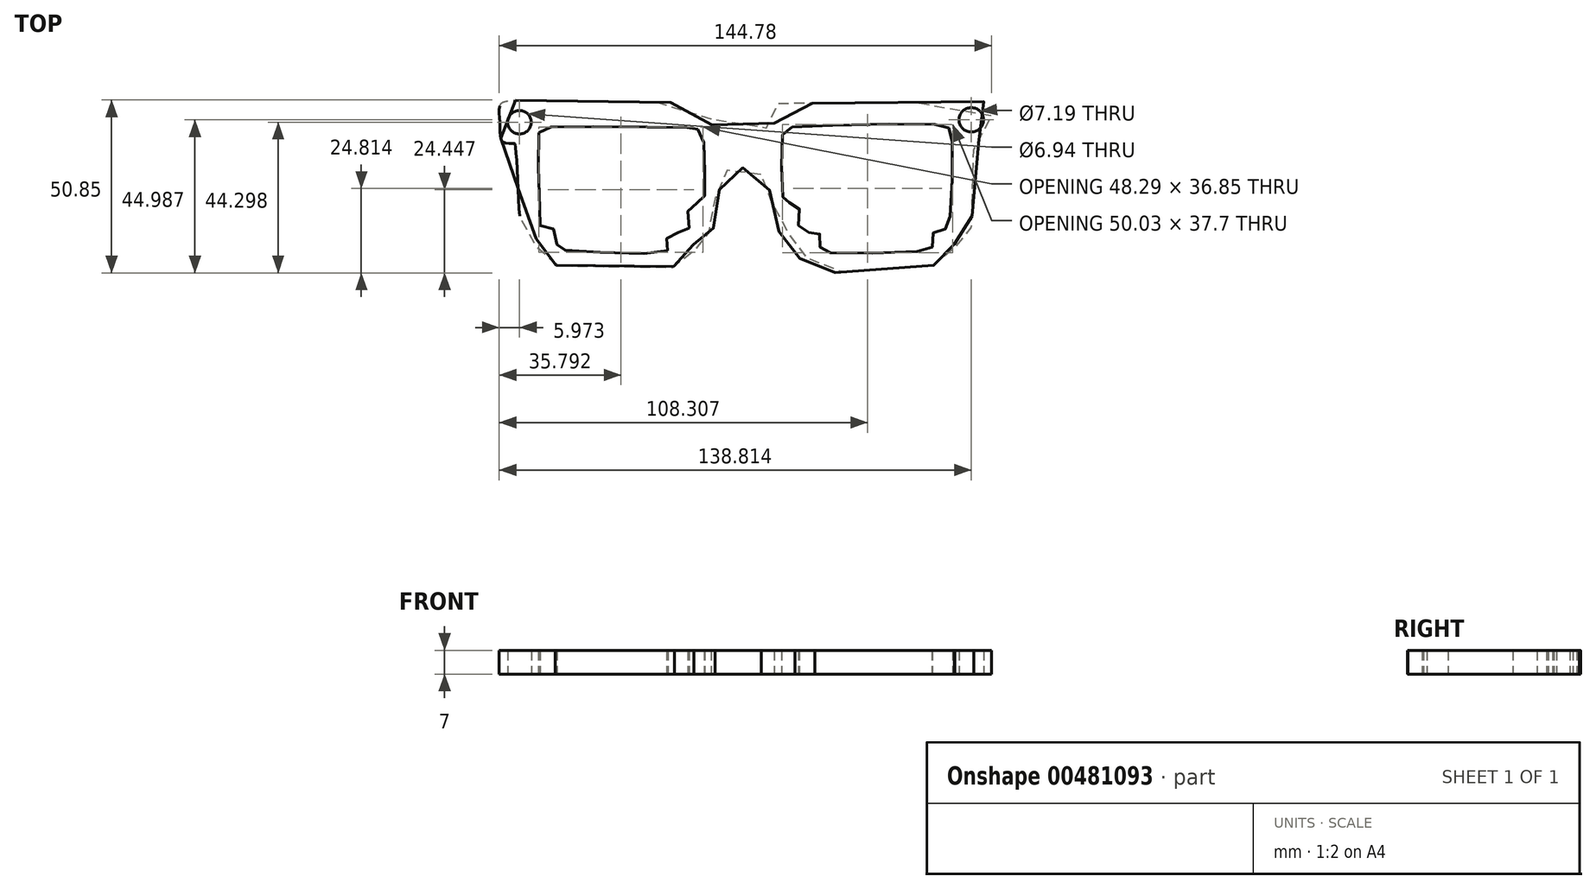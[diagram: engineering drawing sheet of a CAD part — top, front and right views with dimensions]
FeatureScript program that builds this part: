
annotation { "Feature Type Name" : "Feature", "Feature Type Description" : "" }
export const myFeature = defineFeature(function(context is Context, id is Id, definition is map)
    precondition{}
    {
        {
            var Q0;
            Q0=qCreatedBy(makeId("Top.planeOp"),FACE);
            var sketch = newSketch(context, id + "F0", { "sketchPlane" : qUnion([Q0])});
            skFitSpline(sketch, "E0", {"points": [v(-68.04, 23.7) * mm, v(-16.13, 22.84) * mm, v(-10.61, 21.3) * mm, v(-10.5, 16.99) * mm, v(-8.77, 16.08) * mm, v(7.29, 15.82) * mm, v(8.05, 16.84) * mm, v(8.26, 22.25) * mm, v(8.68, 22.78) * mm, v(11.27, 22.78) * mm, v(70.16, 23.26) * mm, v(71.69, 21.97) * mm, v(70.69, 11.67) * mm, v(67.2, 10.88) * mm, v(66.62, 6.92) * mm, v(65.93, -13.32) * mm, v(65.42, -14.26) * mm, v(61.6, -15.4) * mm, v(61.04, -17.84) * mm, v(61.06, -19.93) * mm, v(60.72, -20.9) * mm, v(56.08, -21.78) * mm, v(55.25, -24.5) * mm, v(37.43, -26.54) * mm, v(20.14, -25.7) * mm, v(20.04, -23.37) * mm, v(17.03, -22.71) * mm, v(14.35, -22.25) * mm, v(13.94, -16.8) * mm, v(11.33, -15.22) * mm, v(8.7, -14.72) * mm, v(7.75, -13.39) * mm, v(7.4, -3.48) * mm, v(7, -2.76) * mm, v(4.45, -2.25) * mm, v(4.14, 2.46) * mm, v(0, 3.85) * mm, v(-4.94, 3.63) * mm, v(-5.96, 2.74) * mm, v(-6.71, -2) * mm, v(-8.8, -2.75) * mm, v(-9.36, -5.73) * mm, v(-9.6, -12.76) * mm, v(-9.74, -13.7) * mm, v(-10.9, -15.05) * mm, v(-12.89, -15.43) * mm, v(-14.83, -15.72) * mm, v(-15.78, -16.54) * mm, v(-15.59, -21.13) * mm, v(-16.91, -22.55) * mm, v(-21.3, -22.67) * mm, v(-21.78, -25.37) * mm, v(-55.94, -24.88) * mm, v(-56.26, -23.92) * mm, v(-56.6, -22.11) * mm, v(-61.37, -20.69) * mm, v(-62.3, -15.58) * mm, v(-65.48, -14.1) * mm, v(-66.66, -11.88) * mm, v(-68.11, 10.64) * mm, v(-68.58, 11.06) * mm, v(-71.73, 11.47) * mm, v(-72.62, 16.2) * mm, v(-72.61, 22.14) * mm, v(-68.04, 23.7) * mm]});
            skFitSpline(sketch, "E1", {"points": [v(-61.2, 14.18) * mm, v(-60.89, -12.2) * mm, v(-60.73, -13.2) * mm, v(-56.6, -14.35) * mm, v(-55.75, -19.49) * mm, v(-52.99, -20.4) * mm, v(-24.15, -20.87) * mm, v(-23.23, -19.33) * mm, v(-23.08, -15.73) * mm, v(-17.79, -14.96) * mm, v(-17.02, -12.9) * mm, v(-16.87, -7.3) * mm, v(-13.19, -6.15) * mm, v(-12.5, -2.39) * mm, v(-13.04, 13.26) * mm, v(-14.8, 15.4) * mm, v(-17.1, 15.7) * mm, v(-58.61, 15.88) * mm, v(-61.2, 14.18) * mm]});
            skFitSpline(sketch, "E2", {"points": [v(13.22, 15.85) * mm, v(57.58, 16.35) * mm, v(59.28, 15.66) * mm, v(60.04, 14.65) * mm, v(59.74, -10.84) * mm, v(58.37, -14.17) * mm, v(54.97, -14.99) * mm, v(54.5, -19.26) * mm, v(53.33, -20.33) * mm, v(22.4, -20.85) * mm, v(21.56, -19.8) * mm, v(21.41, -15.85) * mm, v(21.08, -15.22) * mm, v(16.32, -14.83) * mm, v(15.2, -11.72) * mm, v(14.85, -6.88) * mm, v(11.33, -6.27) * mm, v(10.54, -4.96) * mm, v(10.57, 14.33) * mm, v(13.22, 15.85) * mm]});
            skPoint(sketch, "E3", {"position": v(71.78, 14.8) * mm});
            skCircle(sketch, "E4", {"center": v(65.97, 17.96) * mm, "radius": 3.6 * mm});
            skCircle(sketch, "E5", {"center": v(-66.87, 17.27) * mm, "radius": 3.47 * mm});
            skSolve(sketch);
        }
        {
            var Q0;
            Q0 = qSketchRegion(id + "F0", true);
            extrude(context, id + "F1", {"entities" : qUnion([Q0]), "depth" : 7 * mm});
        }
    });
